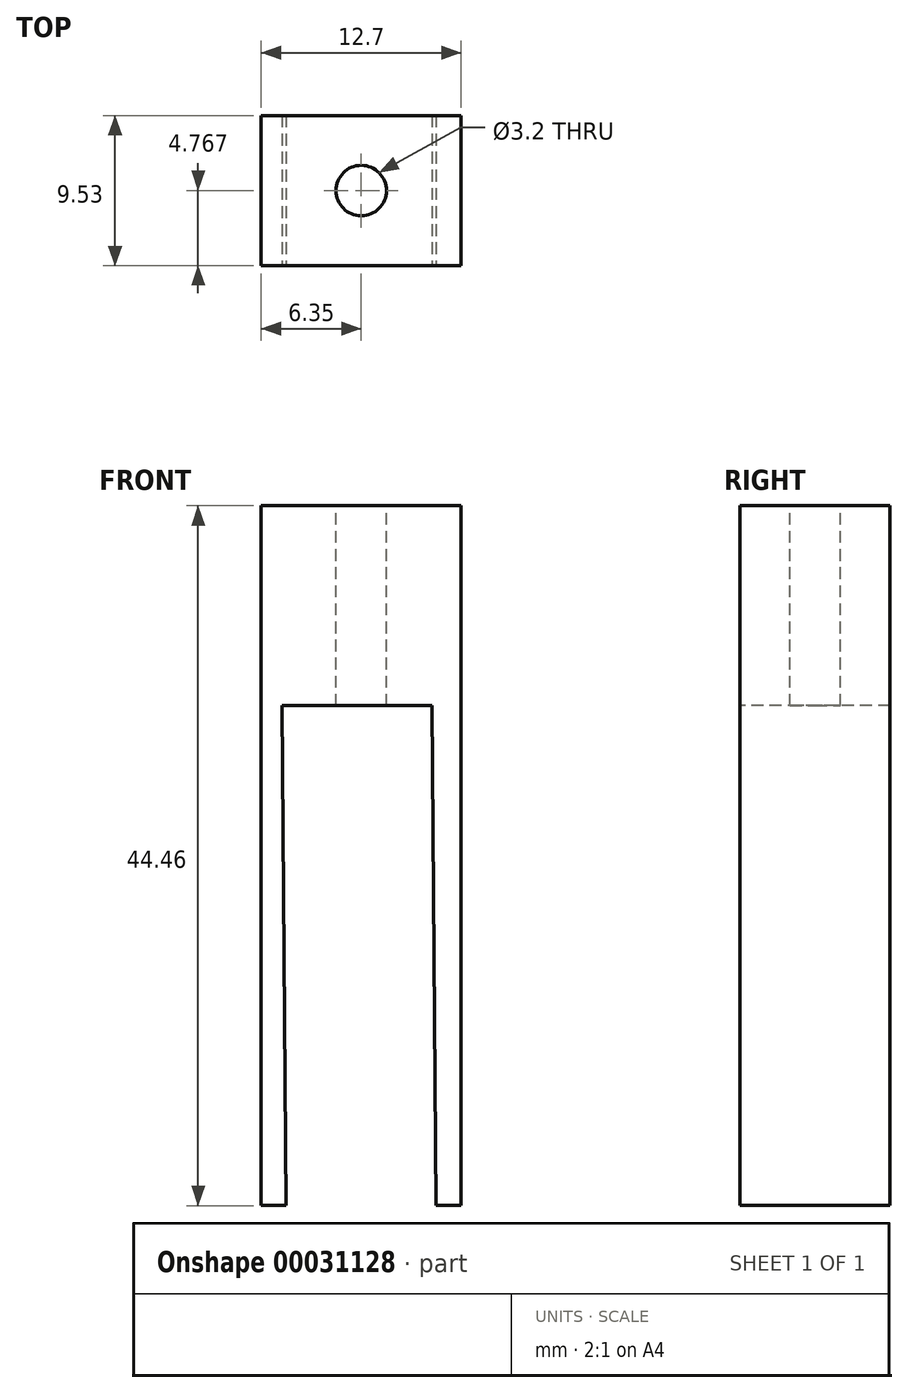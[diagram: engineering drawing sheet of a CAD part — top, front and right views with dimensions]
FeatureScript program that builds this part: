
annotation { "Feature Type Name" : "Feature", "Feature Type Description" : "" }
export const myFeature = defineFeature(function(context is Context, id is Id, definition is map)
    precondition{}
    {
        {
            var Q0;
            Q0=qCreatedBy(makeId("Front.planeOp"),FACE);
            var sketch = newSketch(context, id + "F0", { "sketchPlane" : qUnion([Q0])});
            skLineSegment(sketch, "E0.rect.bottom", {"start": v(6.35, -22.23) * mm, "end": v(-6.35, -22.23) * mm});
            skLineSegment(sketch, "E0.rect.top", {"start": v(6.35, 22.23) * mm, "end": v(-6.35, 22.23) * mm});
            skLineSegment(sketch, "E0.rect.left", {"start": v(6.35, -22.23) * mm, "end": v(6.35, 22.23) * mm});
            skLineSegment(sketch, "E0.rect.right", {"start": v(-6.35, -22.23) * mm, "end": v(-6.35, 22.23) * mm});
            skPoint(sketch, "E0.rect.middle", {"position": v(0, 0) * mm});
            skSolve(sketch);
        }
        {
            var Q0;
            Q0 = qSketchRegion(id + "F0", true);
            extrude(context, id + "F1", {"entities" : qUnion([Q0]), "depth" : 9.52 * mm});
        }
        {
            var Q0;
            Q0=makeQuery(id+"F1.opExtrude","SWEPT_FACE",FACE,{"disambiguationData":[OSD([sQuery(id+"F0.wireOp",EDGE,"E0.rect.top")])]});
            var sketch = newSketch(context, id + "F2", { "sketchPlane" : qUnion([Q0])});
            skCircle(sketch, "E1", {"center": v(0, -4.76) * mm, "radius": 1.6 * mm});
            skSolve(sketch);
        }
        {
            var Q0;
            Q0=makeQuery(id+"F2.imprint","IMPRINT",FACE,{"disambiguationData":[TD([[makeQuery(id+"F2.imprint","IMPRINT",EDGE,{"derivedFrom":sQuery(id+"F2.wireOp",EDGE,"E1")}),1.0]])]});
            extrude(context, id + "F3", {"entities" : qUnion([Q0]), "operationType" : NewBodyOperationType.REMOVE, "oppositeDirection" : true, "depth" : 25.4 * mm});
        }
        {
            var Q0;
            Q0=makeQuery(id+"F1.opExtrude","CAP_FACE",FACE,{"disambiguationData":[OSD([sQuery(id+"F0.wireOp",EDGE,"E0.rect.bottom"),sQuery(id+"F0.wireOp",EDGE,"E0.rect.top"),sQuery(id+"F0.wireOp",EDGE,"E0.rect.left"),sQuery(id+"F0.wireOp",EDGE,"E0.rect.right")])],"isStart":false});
            var sketch = newSketch(context, id + "F4", { "sketchPlane" : qUnion([Q0])});
            skLineSegment(sketch, "E2.rect.bottom", {"start": v(4.5, 9.52) * mm, "end": v(-5.03, 9.52) * mm});
            skLineSegment(sketch, "E2.rect.left", {"start": v(4.5, 9.52) * mm, "end": v(4.76, -22.22) * mm});
            skLineSegment(sketch, "E2.rect.right", {"start": v(-5.03, 9.52) * mm, "end": v(-4.76, -22.23) * mm});
            skPoint(sketch, "E2.rect.middle", {"position": v(0, -22.23) * mm});
            skLineSegment(sketch, "E3", {"start": v(-4.76, -22.23) * mm, "end": v(4.76, -22.22) * mm});
            skPoint(sketch, "E2.rect.top.end.orphan", {"position": v(-4.5, -53.97) * mm});
            skPoint(sketch, "E2.rect.top.start.orphan", {"position": v(5.03, -53.97) * mm});
            skSolve(sketch);
        }
        {
            var Q0;
            {var subQ6=sQuery(id+"F4.wireOp",EDGE,"E2.rect.bottom");Q0=makeQuery(id+"F4.imprint","IMPRINT",FACE,{"disambiguationData":[TD([[makeQuery(id+"F4.imprint","IMPRINT",EDGE,{"derivedFrom":subQ6}),1.0]])]});}
            extrude(context, id + "F5", {"entities" : qUnion([Q0]), "operationType" : NewBodyOperationType.REMOVE, "oppositeDirection" : true, "depth" : 25.4 * mm});
        }
    });
